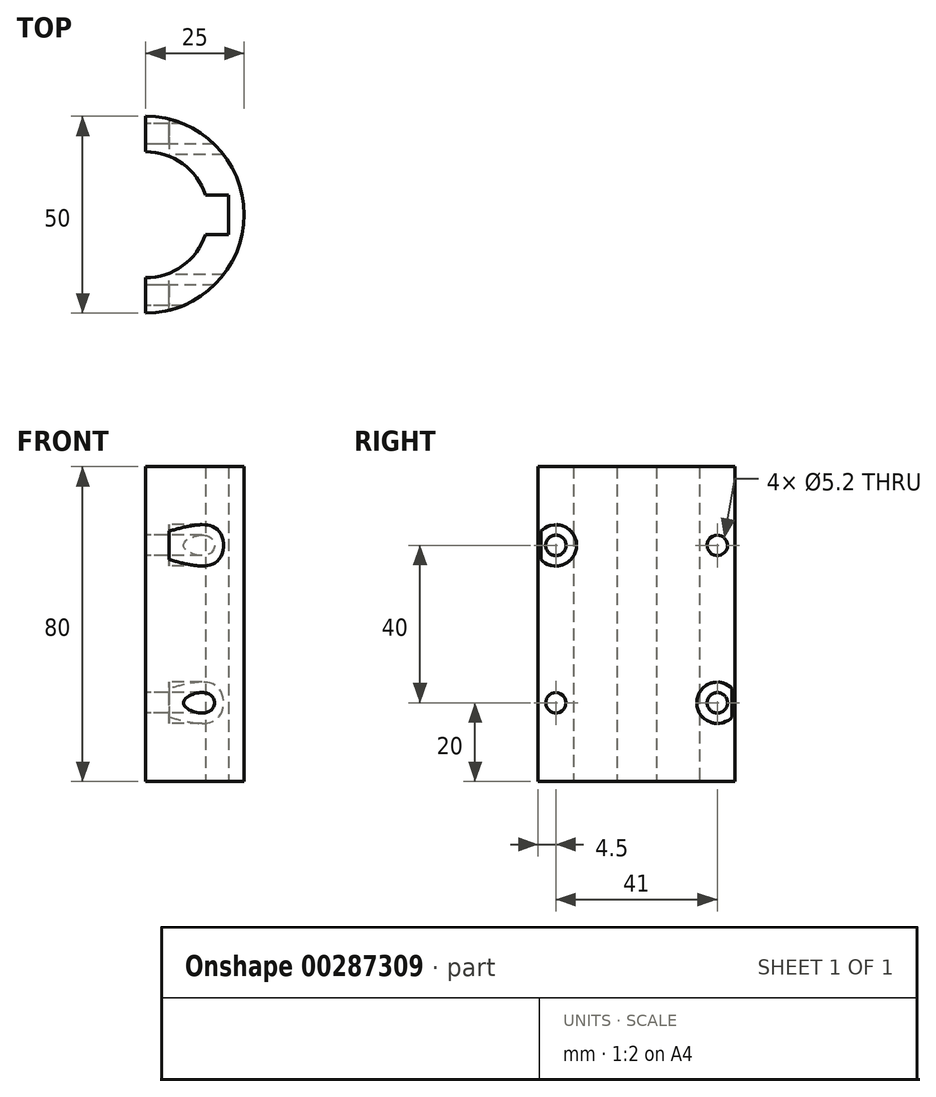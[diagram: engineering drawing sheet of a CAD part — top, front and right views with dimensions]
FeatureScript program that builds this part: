
annotation { "Feature Type Name" : "Feature", "Feature Type Description" : "" }
export const myFeature = defineFeature(function(context is Context, id is Id, definition is map)
    precondition{}
    {
        {
            var Q0;
            Q0=qCreatedBy(makeId("Top.planeOp"),FACE);
            var sketch = newSketch(context, id + "F0", { "sketchPlane" : qUnion([Q0])});
            skArc(sketch, "E0", {"start": v(0, -25) * mm, "mid": v(25, 0) * mm, "end": v(0, 25) * mm});
            skArc(sketch, "E1", {"start": v(0, -16) * mm, "mid": v(16, 0) * mm, "end": v(0, 16) * mm});
            skLineSegment(sketch, "E2", {"start": v(0, 25) * mm, "end": v(0, 16) * mm});
            skLineSegment(sketch, "E3", {"start": v(0, -16) * mm, "end": v(0, -25) * mm});
            skSolve(sketch);
        }
        {
            var Q0;
            Q0 = qSketchRegion(id + "F0", true);
            extrude(context, id + "F1", {"entities" : qUnion([Q0]), "depth" : 80 * mm});
        }
        {
            var Q0;
            Q0=qCreatedBy(makeId("Right.planeOp"),FACE);
            var sketch = newSketch(context, id + "F2", { "sketchPlane" : qUnion([Q0])});
            skCircle(sketch, "E4", {"center": v(-20.5, 20) * mm, "radius": 2.6 * mm});
            skCircle(sketch, "E5", {"center": v(-20.5, 60) * mm, "radius": 2.6 * mm});
            skCircle(sketch, "E6", {"center": v(20.5, 60) * mm, "radius": 2.6 * mm});
            skCircle(sketch, "E7", {"center": v(20.5, 20) * mm, "radius": 2.6 * mm});
            skSolve(sketch);
        }
        {
            var Q0;
            Q0 = qSketchRegion(id + "F2", true);
            extrude(context, id + "F3", {"entities" : qUnion([Q0]), "operationType" : NewBodyOperationType.REMOVE, "endBound" : BoundingType.THROUGH_ALL, "depth" : 25 * mm});
        }
        {
            var Q0;
            Q0=makeQuery(id+"F1.opExtrude","SWEPT_FACE",FACE,{"disambiguationData":[OSD([sQuery(id+"F0.wireOp",EDGE,"E3")])]});
            cPlane(context, id + "F4", {"entities" : qUnion([Q0]), "cplaneType" : CPlaneType.OFFSET, "offset" : 6 * mm, "oppositeDirection" : true, "width" : 150 * mm, "height" : 150 * mm});
        }
        {
            var Q0;
            Q0=qCreatedBy(id+"F4.planeOp",FACE);
            var sketch = newSketch(context, id + "F5", { "sketchPlane" : qUnion([Q0])});
            skCircle(sketch, "E8", {"center": v(20.5, 60) * mm, "radius": 5.25 * mm});
            skLineSegment(sketch, "E9", {"start": v(20.5, 60) * mm, "end": v(-20.5, 60) * mm});
            skCircle(sketch, "E10", {"center": v(-20.5, 20) * mm, "radius": 5.25 * mm});
            skLineSegment(sketch, "E11", {"start": v(-20.5, 60) * mm, "end": v(-20.5, 20) * mm});
            skSolve(sketch);
        }
        {
            var Q0;
            Q0 = qSketchRegion(id + "F5", true);
            extrude(context, id + "F6", {"entities" : qUnion([Q0]), "operationType" : NewBodyOperationType.REMOVE, "oppositeDirection" : true, "depth" : 25 * mm});
        }
        {
            var Q0;
            Q0=qCreatedBy(makeId("Top.planeOp"),FACE);
            var sketch = newSketch(context, id + "F7", { "sketchPlane" : qUnion([Q0])});
            skLineSegment(sketch, "E12.bottom", {"start": v(21, 5) * mm, "end": v(11, 5) * mm});
            skLineSegment(sketch, "E12.top", {"start": v(21, -5) * mm, "end": v(11, -5) * mm});
            skLineSegment(sketch, "E12.left", {"start": v(21, 5) * mm, "end": v(21, -5) * mm});
            skLineSegment(sketch, "E12.right", {"start": v(11, 5) * mm, "end": v(11, -5) * mm});
            skPoint(sketch, "E12.middle", {"position": v(16, 0) * mm});
            skSolve(sketch);
        }
        {
            var Q0;
            Q0 = qSketchRegion(id + "F7", true);
            extrude(context, id + "F8", {"entities" : qUnion([Q0]), "operationType" : NewBodyOperationType.REMOVE, "endBound" : BoundingType.THROUGH_ALL, "depth" : 25 * mm});
        }
    });
